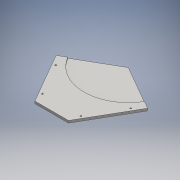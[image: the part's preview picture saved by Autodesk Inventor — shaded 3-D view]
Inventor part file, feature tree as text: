
AUTODESK INVENTOR PART (.ipt)
format: ipt  version: 2016 SP1 (Build 200210100, 210)  size: 135,680 bytes
history: native  units: mm
features: reference x3, extrude x2, sketch x2
ambient origin geometry x8: Origin, YZ Plane, XZ Plane, XY Plane, X Axis, Y Axis, Z Axis, Center Point
bodies: Solid1 (feature_tree)
feature tree (7):
  extrude  "Extrusion1"  Depth=5.0mm
  extrude  "Extrusion2"  Depth=5.0mm
  sketch  "Sketch1"  dims[d0=5.0mm d1=5.0mm]
  reference  "Reference2"
  reference  "Reference3"
  sketch  "Sketch2"  dims[d2=5.0mm d3=5.0mm d4=10.0mm d5=10.0mm d6=10.0mm d7=10.0mm d8=40.0mm d9=40.0mm d10=125.0mm d11=125.0mm d12=8.0mm d13=0.0mm d14=3.0mm d15=0.0mm]
  reference  "Reference4"
